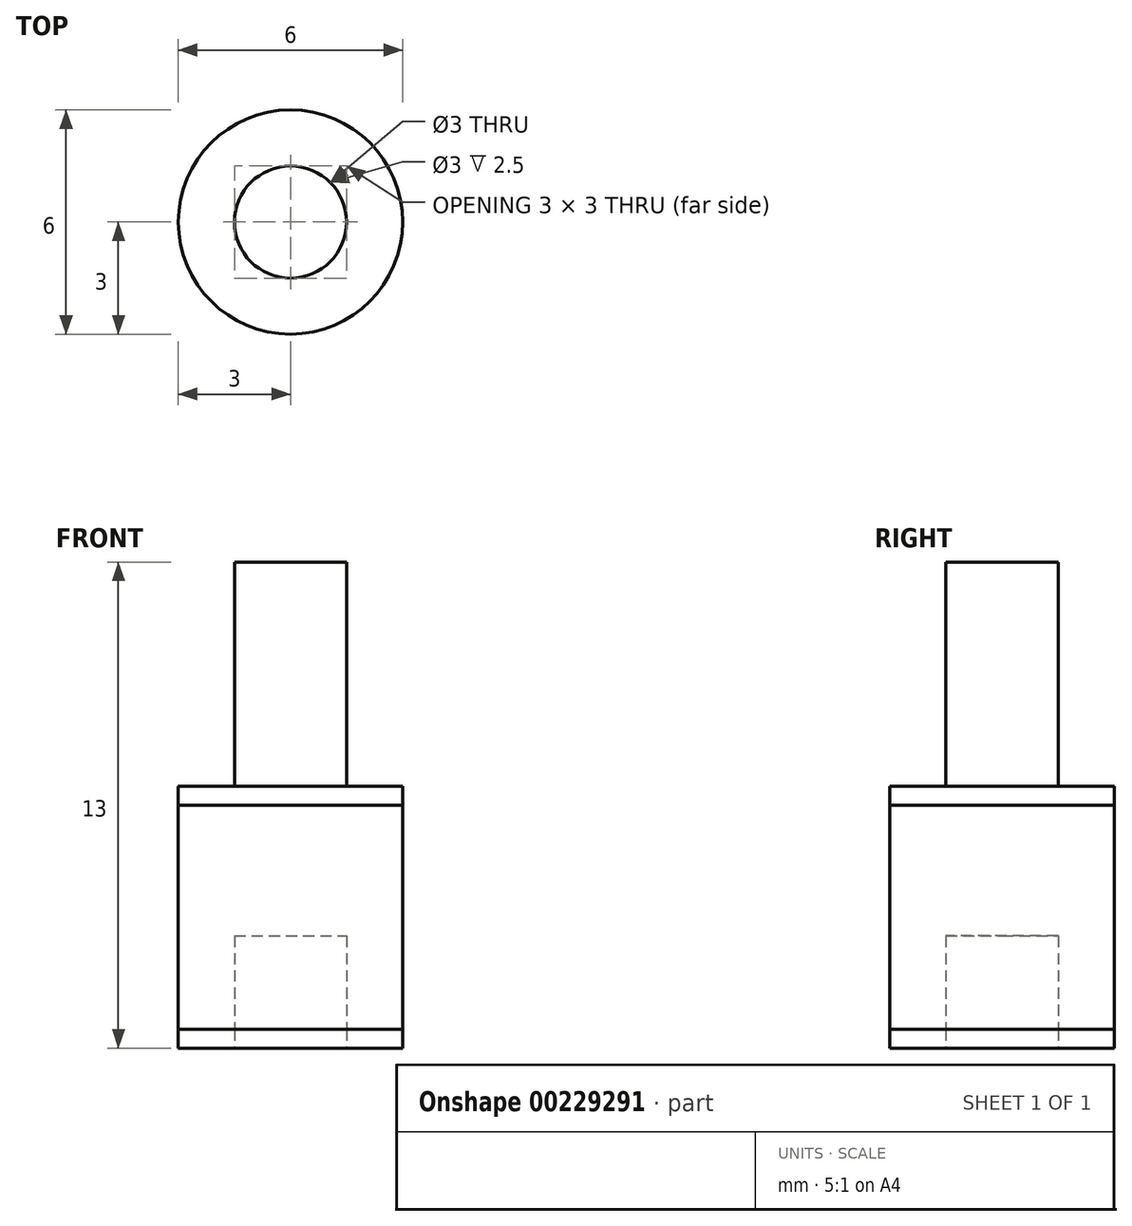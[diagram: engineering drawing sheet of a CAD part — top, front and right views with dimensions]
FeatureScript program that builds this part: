
annotation { "Feature Type Name" : "Feature", "Feature Type Description" : "" }
export const myFeature = defineFeature(function(context is Context, id is Id, definition is map)
    precondition{}
    {
        {
            assignVariable(context, id + "F0", {"name" : "DelkaSroubu", "anyValue" : 6});
        }
        {
            assignVariable(context, id + "F1", {"name" : "VyskaBloku", "anyValue" : 7});
        }
        {
            assignVariable(context, id + "F2", {"name" : "HloubkaDiry", "anyValue" : 3});
        }
        {
            assignVariable(context, id + "F3", {"name" : "TloustkaPlatu", "anyValue" : 0.5});
        }
        {
            var Q0;
            Q0=qCreatedBy(makeId("Top.planeOp"),FACE);
            var sketch = newSketch(context, id + "F4", { "sketchPlane" : qUnion([Q0])});
            skCircle(sketch, "E0", {"center": v(0, 0) * mm, "radius": 3 * mm});
            skSolve(sketch);
        }
        {
            var Q0;
            Q0=makeQuery(id+"F4.imprint","IMPRINT",FACE,{"disambiguationData":[TD([[makeQuery(id+"F4.imprint","IMPRINT",EDGE,{"derivedFrom":sQuery(id+"F4.wireOp",EDGE,"E0")}),1.0]])]});
            var Q1;
            Q1=sQuery(id+"F4.wireOp",EDGE,"E0");
            extrude(context, id + "F5", {"entities" : qUnion([Q0]), "surfaceEntities" : qUnion([Q1]), "endBound" : BoundingType.SYMMETRIC, "depth" : (getVariable(context, 'VyskaBloku') - 2 * getVariable(context, 'TloustkaPlatu')) * mm});
        }
        {
            var Q0;
            Q0=makeQuery(id+"F5.opExtrude","CAP_FACE",FACE,{"disambiguationData":[OSD([sQuery(id+"F4.wireOp",EDGE,"E0")])],"isStart":false});
            extrude(context, id + "F6", {"entities" : qUnion([Q0]), "depth" : (getVariable(context, 'TloustkaPlatu')) * mm});
        }
        {
            var Q0;
            Q0=makeQuery(id+"F5.opExtrude","CAP_FACE",FACE,{"disambiguationData":[OSD([sQuery(id+"F4.wireOp",EDGE,"E0")])],"isStart":true});
            extrude(context, id + "F7", {"entities" : qUnion([Q0]), "depth" : (getVariable(context, 'TloustkaPlatu')) * mm});
        }
        {
            var Q0;
            Q0=makeQuery(id+"F6.opExtrude","CAP_FACE",FACE,{"disambiguationData":[OSD([sQuery(id+"F4.wireOp",EDGE,"E0")])],"isStart":false});
            var sketch = newSketch(context, id + "F8", { "sketchPlane" : qUnion([Q0])});
            skCircle(sketch, "E1", {"center": v(0, 0) * mm, "radius": 1.5 * mm});
            skSolve(sketch);
        }
        {
            var Q0;
            Q0=makeQuery(id+"F8.imprint","IMPRINT",FACE,{"disambiguationData":[TD([[makeQuery(id+"F8.imprint","IMPRINT",EDGE,{"derivedFrom":sQuery(id+"F8.wireOp",EDGE,"E1")}),1.0]])]});
            extrude(context, id + "F9", {"entities" : qUnion([Q0]), "operationType" : NewBodyOperationType.ADD, "depth" : (getVariable(context, 'DelkaSroubu')) * mm});
        }
        {
            var Q0;
            Q0=makeQuery(id+"F7.opExtrude","CAP_FACE",FACE,{"disambiguationData":[OSD([sQuery(id+"F4.wireOp",EDGE,"E0")])],"isStart":false});
            var sketch = newSketch(context, id + "F10", { "sketchPlane" : qUnion([Q0])});
            skCircle(sketch, "E2", {"center": v(0, 0) * mm, "radius": 1.5 * mm});
            skSolve(sketch);
        }
        {
            var Q0;
            Q0 = qSketchRegion(id + "F10", true);
            extrude(context, id + "F11", {"entities" : qUnion([Q0]), "oppositeDirection" : true, "depth" : (getVariable(context, 'HloubkaDiry')) * mm});
        }
        {
            var Q0;
            Q0=makeQuery(id+"F11.opExtrude","SWEPT_BODY",BODY,{"disambiguationData":[OSD([sQuery(id+"F10.wireOp",EDGE,"E2")])]});
            var Q1;
            Q1=makeQuery(id+"F7.opExtrude","SWEPT_BODY",BODY,{"disambiguationData":[OSD([sQuery(id+"F4.wireOp",EDGE,"E0")])]});
            var Q2;
            Q2=makeQuery(id+"F5.opExtrude","SWEPT_BODY",BODY,{"disambiguationData":[OSD([sQuery(id+"F4.wireOp",EDGE,"E0")])]});
            booleanBodies(context, id + "F12", {"operationType" : BooleanOperationType.SUBTRACTION, "tools" : qUnion([Q0]), "targets" : qUnion([Q1, Q2])});
        }
    });
